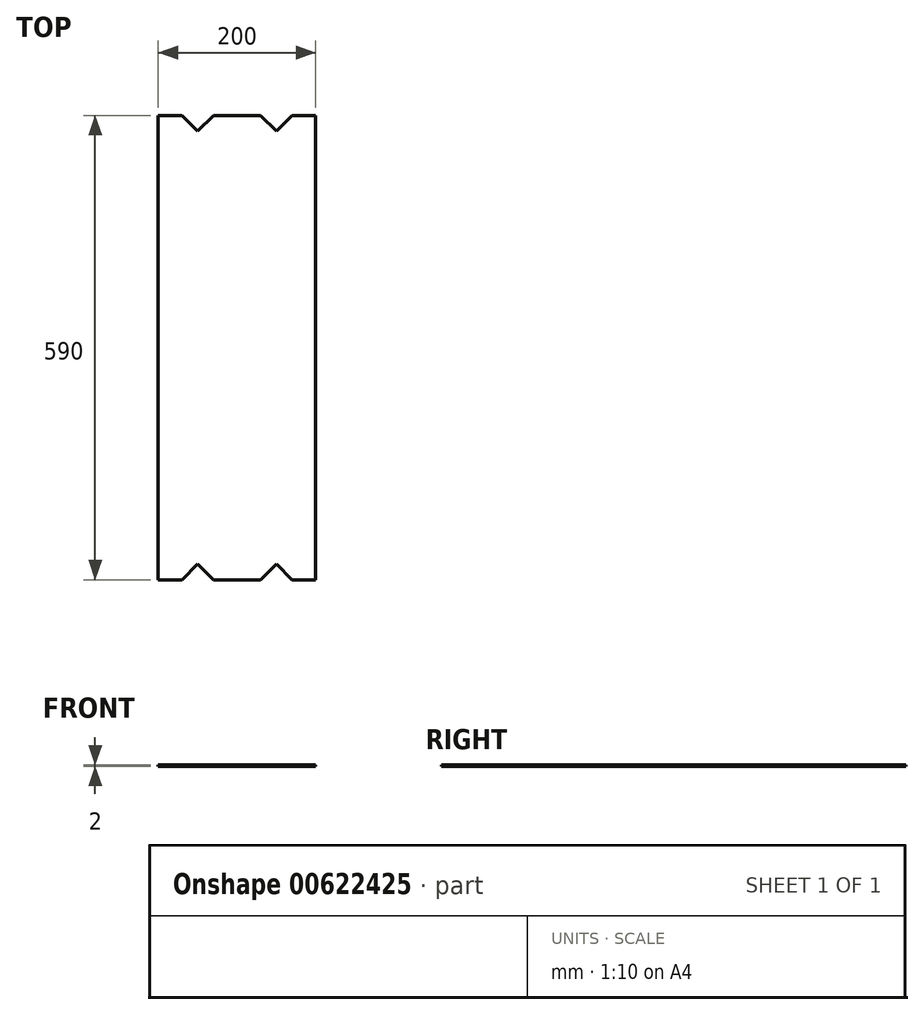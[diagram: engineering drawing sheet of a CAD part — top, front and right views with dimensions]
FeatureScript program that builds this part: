
annotation { "Feature Type Name" : "Feature", "Feature Type Description" : "" }
export const myFeature = defineFeature(function(context is Context, id is Id, definition is map)
    precondition{}
    {
        {
            var Q0;
            Q0=qCreatedBy(makeId("Top.planeOp"),FACE);
            var sketch = newSketch(context, id + "F0", { "sketchPlane" : qUnion([Q0])});
            skLineSegment(sketch, "E0", {"start": v(-47.87, 0) * mm, "end": v(152.13, 0) * mm});
            skLineSegment(sketch, "E1", {"start": v(152.13, 0) * mm, "end": v(152.13, 70) * mm});
            skPoint(sketch, "E2", {"position": v(102.13, 50) * mm});
            skPoint(sketch, "E3", {"position": v(2.13, 50) * mm});
            skLineSegment(sketch, "E4", {"start": v(152.13, 70) * mm, "end": v(122.13, 70) * mm});
            skLineSegment(sketch, "E5", {"start": v(122.13, 70) * mm, "end": v(102.13, 50) * mm});
            skLineSegment(sketch, "E6", {"start": v(-47.87, 0) * mm, "end": v(-47.87, 70) * mm});
            skLineSegment(sketch, "E7", {"start": v(-47.87, 70) * mm, "end": v(-17.87, 70) * mm});
            skLineSegment(sketch, "E8", {"start": v(-17.87, 70) * mm, "end": v(2.13, 50) * mm});
            skPoint(sketch, "E9", {"position": v(102.13, 70) * mm});
            skPoint(sketch, "E10", {"position": v(2.13, 70) * mm});
            skPoint(sketch, "E11", {"position": v(22.13, 70) * mm});
            skPoint(sketch, "E12", {"position": v(82.13, 70) * mm});
            skLineSegment(sketch, "E13", {"start": v(2.13, 50) * mm, "end": v(22.13, 70) * mm});
            skLineSegment(sketch, "E14", {"start": v(82.13, 70) * mm, "end": v(22.13, 70) * mm});
            skLineSegment(sketch, "E15", {"start": v(82.13, 70) * mm, "end": v(102.13, 50) * mm});
            skLineSegment(sketch, "E16.filletArc", {"start": v(2.13, 50) * mm, "end": v(2.13, 50) * mm});
            skLineSegment(sketch, "E17.filletArc", {"start": v(102.13, 50) * mm, "end": v(102.13, 50) * mm});
            skLineSegment(sketch, "E18", {"start": v(-47.87, 0) * mm, "end": v(-47.87, -450) * mm});
            skLineSegment(sketch, "E19", {"start": v(-47.87, -450) * mm, "end": v(152.13, -450) * mm});
            skLineSegment(sketch, "E20", {"start": v(152.13, -450) * mm, "end": v(152.13, 0) * mm});
            skLineSegment(sketch, "E21", {"start": v(-47.87, -450) * mm, "end": v(-47.87, -520) * mm});
            skLineSegment(sketch, "E22", {"start": v(152.13, -450) * mm, "end": v(152.13, -520) * mm});
            skLineSegment(sketch, "E23", {"start": v(-47.87, -520) * mm, "end": v(-17.87, -520) * mm});
            skLineSegment(sketch, "E24", {"start": v(152.13, -520) * mm, "end": v(122.13, -520) * mm});
            skPoint(sketch, "E25", {"position": v(2.13, -500) * mm});
            skPoint(sketch, "E26", {"position": v(102.13, -500) * mm});
            skPoint(sketch, "E27", {"position": v(22.13, -520) * mm});
            skLineSegment(sketch, "E28", {"start": v(-17.87, -520) * mm, "end": v(2.13, -500) * mm});
            skLineSegment(sketch, "E29", {"start": v(22.13, -520) * mm, "end": v(2.13, -500) * mm});
            skPoint(sketch, "E30", {"position": v(82.13, -520) * mm});
            skLineSegment(sketch, "E31", {"start": v(122.13, -520) * mm, "end": v(102.13, -500) * mm});
            skLineSegment(sketch, "E32", {"start": v(82.13, -520) * mm, "end": v(102.13, -500) * mm});
            skLineSegment(sketch, "E33", {"start": v(82.13, -520) * mm, "end": v(22.13, -520) * mm});
            skLineSegment(sketch, "E34.filletArc", {"start": v(2.13, -500) * mm, "end": v(2.13, -500) * mm});
            skLineSegment(sketch, "E35.filletArc", {"start": v(102.13, -500) * mm, "end": v(102.13, -500) * mm});
            skSolve(sketch);
        }
        {
            var Q0;
            Q0 = qSketchRegion(id + "F0", true);
            extrude(context, id + "F1", {"entities" : qUnion([Q0]), "depth" : 2 * mm, "offsetDistance" : 25 * mm});
        }
    });
